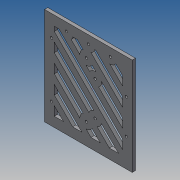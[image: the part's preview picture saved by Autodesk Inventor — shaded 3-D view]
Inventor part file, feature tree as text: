
AUTODESK INVENTOR PART (.ipt)
format: ipt  version: 2017 (Build 210142000, 142)  size: 224,768 bytes
history: native  units: mm
features: reference x17, other x9, extrude x5, sketch x5, projected_geometry x1
ambient origin geometry x8: Origin, YZ Plane, XZ Plane, XY Plane, X Axis, Y Axis, Z Axis, Center Point
bodies: Body1 (feature_tree)
feature tree (37):
  other  "Sólido1"
  extrude  "Extrusión1"  Depth=120.0mm
  sketch  "Boceto2"  dims[d6=4.0mm d7=0.0mm d9=28.0mm]
  extrude  "Extrusión2"  Depth=4.0mm
  extrude  "Extrusión3"  Depth=10.0mm
  extrude  "Extrusión4"  Depth=12.0mm
  extrude  "Extrusión5"  TaperAngle=45.0deg  [1 undecoded]
  sketch  "Boceto1"  dims[d0=108.0mm d1=120.0mm]
  reference  "Referencia1"
  reference  "Referencia2"
  reference  "Referencia3"
  reference  "Referencia4"
  reference  "Referencia5"
  reference  "Referencia6"
  reference  "Referencia7"
  reference  "Referencia8"
  sketch  "Boceto3"  dims[d10=3.0mm d11=10.0mm]
  projected_geometry  "Contorno proyectado1"
  sketch  "Boceto4"  dims[d12=12.0mm d13=12.0mm]
  reference  "Referencia9"
  reference  "Referencia10"
  reference  "Referencia11"
  reference  "Referencia12"
  sketch  "Boceto5"  dims[d14=12.0mm d15=45.0deg d16=8.0mm d17=8.0mm d18=8.0mm d19=8.0mm d20=8.0mm d21=8.0mm d22=8.0mm d23=8.0mm d24=8.0mm d25=8.0mm d26=8.0mm d27=8.0mm d28=8.0mm d29=8.0mm d30=8.0mm d31=10.0mm d32=0.0mm d33=14.0mm d34=4.0mm d35=0.0mm d36=10.0mm d37=0.0mm d38=10.0mm d39=0.0mm]
  reference  "Referencia13"
  reference  "Referencia14"
  reference  "Referencia15"
  reference  "Referencia16"
  reference  "Referencia17"
  other  "<userpath>\Documents\GitHub\actor-re-actor\models\inventor-caja\Piezas\componentes.iam"
  other  "componentes.iam"
  other  "driver motor:1"
  other  "dimmer:1"
  other  "<userpath>\Documents\GitHub\actor-re-actor\models\inventor-caja\ensamble caja motriz.iam"
  other  "ensamble caja motriz.iam"
  other  "Case-D:1"
  other  "Carcasa:1"
note: 1 required parameter value undecoded (feature->parameter linkage not recoverable at this tier; creation-order binding heuristic only, values carry confidence <= 0.55)
